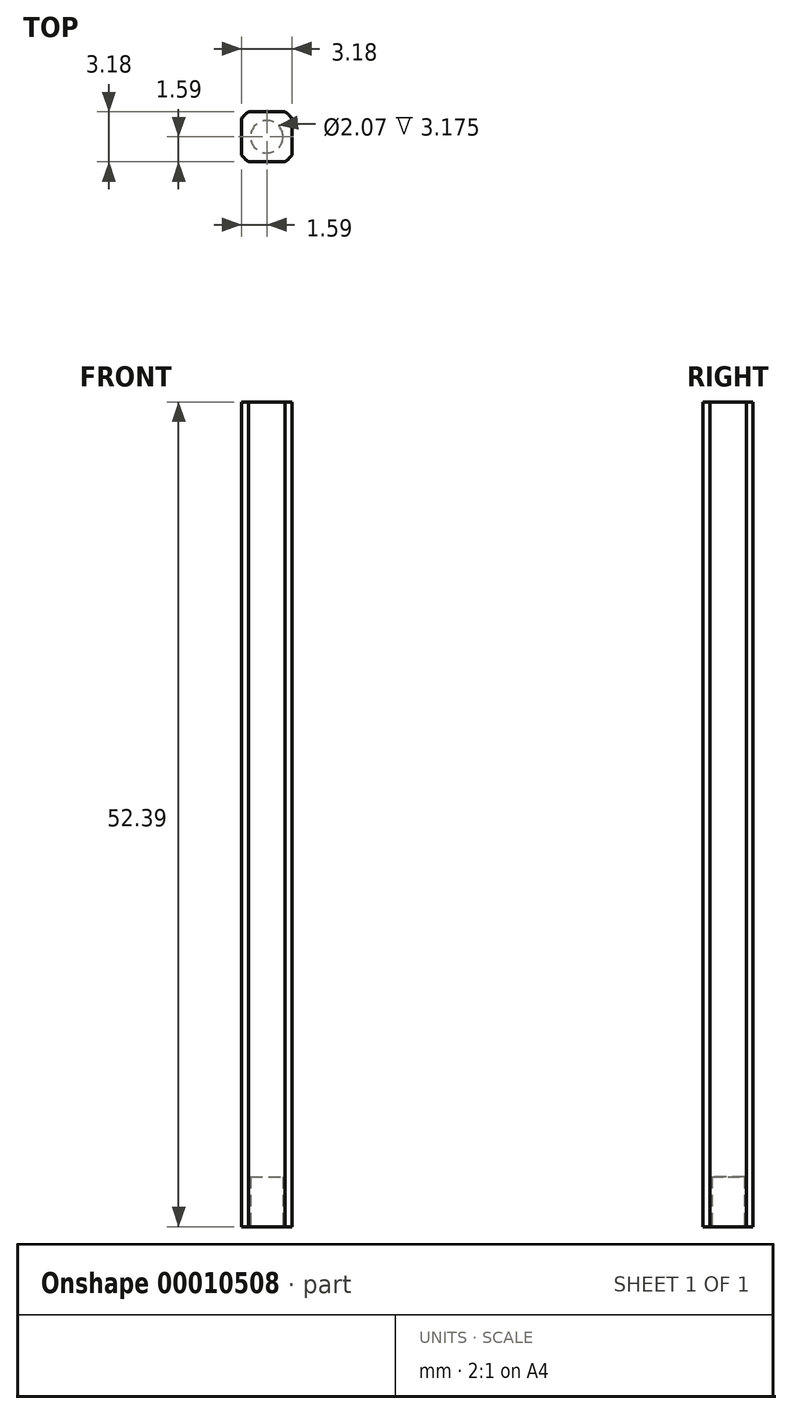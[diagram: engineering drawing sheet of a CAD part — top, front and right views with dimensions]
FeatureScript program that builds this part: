
annotation { "Feature Type Name" : "Feature", "Feature Type Description" : "" }
export const myFeature = defineFeature(function(context is Context, id is Id, definition is map)
    precondition{}
    {
        {
            var Q0;
            Q0=qCreatedBy(makeId("Top.planeOp"),FACE);
            var sketch = newSketch(context, id + "F0", { "sketchPlane" : qUnion([Q0])});
            skLineSegment(sketch, "E0.rect.bottom", {"start": v(1.16, 1.59) * mm, "end": v(-1.16, 1.59) * mm});
            skLineSegment(sketch, "E0.rect.top", {"start": v(1.16, -1.59) * mm, "end": v(-1.16, -1.59) * mm});
            skLineSegment(sketch, "E0.rect.left", {"start": v(1.59, 1.16) * mm, "end": v(1.59, -1.16) * mm});
            skLineSegment(sketch, "E0.rect.right", {"start": v(-1.59, 1.16) * mm, "end": v(-1.59, -1.16) * mm});
            skPoint(sketch, "E0.rect.middle", {"position": v(0, 0) * mm});
            skArc(sketch, "E1", {"start": v(-1.16, 1.59) * mm, "mid": v(-1.4, 1.4) * mm, "end": v(-1.59, 1.16) * mm});
            skPoint(sketch, "E2.orphan", {"position": v(1.59, 1.59) * mm});
            skPoint(sketch, "E3.orphan", {"position": v(-1.59, 1.59) * mm});
            skArc(sketch, "E4.trimOffspring", {"start": v(-1.59, -1.16) * mm, "mid": v(-1.4, -1.4) * mm, "end": v(-1.16, -1.59) * mm});
            skPoint(sketch, "E5.orphan", {"position": v(-1.59, -1.59) * mm});
            skArc(sketch, "E6.trimOffspring", {"start": v(1.16, -1.59) * mm, "mid": v(1.4, -1.4) * mm, "end": v(1.59, -1.16) * mm});
            skPoint(sketch, "E7.orphan", {"position": v(1.59, -1.59) * mm});
            skArc(sketch, "E8.trimOffspring", {"start": v(1.59, 1.16) * mm, "mid": v(1.4, 1.4) * mm, "end": v(1.16, 1.59) * mm});
            skSolve(sketch);
        }
        {
            var Q0;
            Q0 = qSketchRegion(id + "F0", true);
            extrude(context, id + "F1", {"entities" : qUnion([Q0]), "depth" : 52.4 * mm});
        }
        {
            var Q0;
            Q0=makeQuery(id+"F1.opExtrude","CAP_FACE",FACE,{"disambiguationData":[OSD([sQuery(id+"F0.wireOp",EDGE,"E0.rect.bottom"),sQuery(id+"F0.wireOp",EDGE,"E0.rect.top"),sQuery(id+"F0.wireOp",EDGE,"E0.rect.left"),sQuery(id+"F0.wireOp",EDGE,"E0.rect.right"),sQuery(id+"F0.wireOp",EDGE,"E1"),sQuery(id+"F0.wireOp",EDGE,"E4.trimOffspring"),sQuery(id+"F0.wireOp",EDGE,"E6.trimOffspring"),sQuery(id+"F0.wireOp",EDGE,"E8.trimOffspring")])],"isStart":true});
            var sketch = newSketch(context, id + "F2", { "sketchPlane" : qUnion([Q0])});
            skCircle(sketch, "E9", {"center": v(0, 0) * mm, "radius": 1.03 * mm});
            skSolve(sketch);
        }
        {
            var Q0;
            Q0 = qSketchRegion(id + "F2", true);
            extrude(context, id + "F3", {"entities" : qUnion([Q0]), "operationType" : NewBodyOperationType.REMOVE, "oppositeDirection" : true, "depth" : 3.17 * mm});
        }
    });
